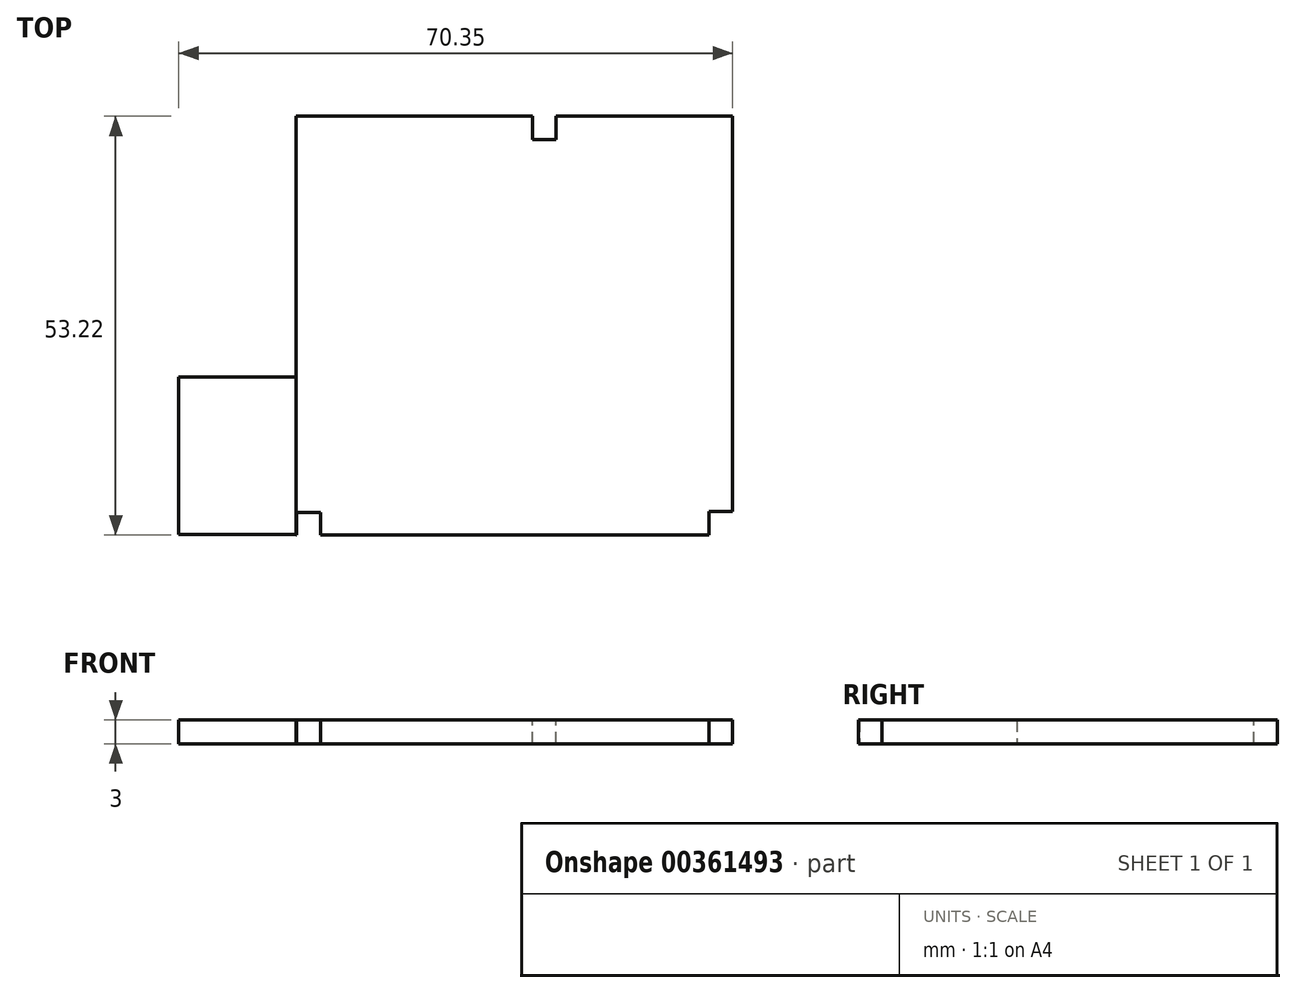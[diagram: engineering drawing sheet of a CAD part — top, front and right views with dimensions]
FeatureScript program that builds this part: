
annotation { "Feature Type Name" : "Feature", "Feature Type Description" : "" }
export const myFeature = defineFeature(function(context is Context, id is Id, definition is map)
    precondition{}
    {
        {
            var Q0;
            Q0=qCreatedBy(makeId("Top.planeOp"),FACE);
            var sketch = newSketch(context, id + "F0", { "sketchPlane" : qUnion([Q0])});
            skLineSegment(sketch, "E0.bottom", {"start": v(-28.37, -22.66) * mm, "end": v(27.04, -22.66) * mm});
            skLineSegment(sketch, "E0.top", {"start": v(-28.37, 30.56) * mm, "end": v(27.04, 30.56) * mm});
            skLineSegment(sketch, "E0.left", {"start": v(-28.37, -22.66) * mm, "end": v(-28.37, 30.56) * mm});
            skLineSegment(sketch, "E0.right", {"start": v(27.04, -22.66) * mm, "end": v(27.04, 30.56) * mm});
            skSolve(sketch);
        }
        {
            var Q0;
            Q0=makeQuery(id+"F0.imprint","IMPRINT",FACE,{"disambiguationData":[TD([[makeQuery(id+"F0.imprint","IMPRINT",EDGE,{"derivedFrom":sQuery(id+"F0.wireOp",EDGE,"E0.bottom")}),1.0]])]});
            var sketch = newSketch(context, id + "F1", { "sketchPlane" : qUnion([Q0])});
            skLineSegment(sketch, "E1.bottom", {"start": v(-43.31, -2.56) * mm, "end": v(-28.31, -2.56) * mm});
            skLineSegment(sketch, "E1.top", {"start": v(-43.31, -22.56) * mm, "end": v(-28.31, -22.56) * mm});
            skLineSegment(sketch, "E1.left", {"start": v(-43.31, -2.56) * mm, "end": v(-43.31, -22.56) * mm});
            skLineSegment(sketch, "E1.right", {"start": v(-28.31, -2.56) * mm, "end": v(-28.31, -22.56) * mm});
            skSolve(sketch);
        }
        {
            var Q0;
            Q0=qCreatedBy(makeId("Top.planeOp"),FACE);
            var sketch = newSketch(context, id + "F2", { "sketchPlane" : qUnion([Q0])});
            skLineSegment(sketch, "E2.bottom", {"start": v(-28.31, -22.76) * mm, "end": v(-25.31, -22.76) * mm});
            skLineSegment(sketch, "E2.top", {"start": v(-28.31, -19.76) * mm, "end": v(-25.31, -19.76) * mm});
            skLineSegment(sketch, "E2.left", {"start": v(-28.31, -22.76) * mm, "end": v(-28.31, -19.76) * mm});
            skLineSegment(sketch, "E2.right", {"start": v(-25.31, -22.76) * mm, "end": v(-25.31, -19.76) * mm});
            skLineSegment(sketch, "E3.bottom", {"start": v(27.04, -22.66) * mm, "end": v(24.04, -22.66) * mm});
            skLineSegment(sketch, "E3.top", {"start": v(27.04, -19.66) * mm, "end": v(24.04, -19.66) * mm});
            skLineSegment(sketch, "E3.left", {"start": v(27.04, -22.66) * mm, "end": v(27.04, -19.66) * mm});
            skLineSegment(sketch, "E3.right", {"start": v(24.04, -22.66) * mm, "end": v(24.04, -19.66) * mm});
            skLineSegment(sketch, "E4.bottom", {"start": v(1.63, 30.56) * mm, "end": v(4.63, 30.56) * mm});
            skLineSegment(sketch, "E4.top", {"start": v(1.63, 27.56) * mm, "end": v(4.63, 27.56) * mm});
            skLineSegment(sketch, "E4.left", {"start": v(1.63, 30.56) * mm, "end": v(1.63, 27.56) * mm});
            skLineSegment(sketch, "E4.right", {"start": v(4.63, 30.56) * mm, "end": v(4.63, 27.56) * mm});
            skSolve(sketch);
        }
        {
            var Q0;
            Q0=makeQuery(id+"F0.imprint","IMPRINT",FACE,{"disambiguationData":[TD([[makeQuery(id+"F0.imprint","IMPRINT",EDGE,{"derivedFrom":sQuery(id+"F0.wireOp",EDGE,"E0.bottom")}),1.0]])]});
            var Q1;
            {var subQ0=sQuery(id+"F1.wireOp",EDGE,"E1.left");Q1=makeQuery(id+"F1.imprint","IMPRINT",FACE,{"disambiguationData":[TD([[makeQuery(id+"F1.imprint","IMPRINT",EDGE,{"derivedFrom":subQ0}),1.0]])]});}
            extrude(context, id + "F3", {"entities" : qUnion([Q0, Q1]), "depth" : 3 * mm});
        }
        {
            var Q0;
            Q0=makeQuery(id+"F2.imprint","IMPRINT",FACE,{"disambiguationData":[TD([[makeQuery(id+"F2.imprint","IMPRINT",EDGE,{"derivedFrom":sQuery(id+"F2.wireOp",EDGE,"E4.bottom")}),-1.0]])]});
            var Q1;
            Q1=makeQuery(id+"F2.imprint","IMPRINT",FACE,{"disambiguationData":[TD([[makeQuery(id+"F2.imprint","IMPRINT",EDGE,{"derivedFrom":sQuery(id+"F2.wireOp",EDGE,"E2.bottom")}),1.0]])]});
            var Q2;
            Q2=makeQuery(id+"F2.imprint","IMPRINT",FACE,{"disambiguationData":[TD([[makeQuery(id+"F2.imprint","IMPRINT",EDGE,{"derivedFrom":sQuery(id+"F2.wireOp",EDGE,"E3.bottom")}),-1.0]])]});
            extrude(context, id + "F4", {"entities" : qUnion([Q0, Q1, Q2]), "operationType" : NewBodyOperationType.ADD, "depth" : 8.2 * mm});
        }
        {
            var Q0;
            Q0=makeQuery(id+"F4.opExtrude","CAP_FACE",FACE,{"disambiguationData":[OSD([sQuery(id+"F2.wireOp",EDGE,"E4.bottom"),sQuery(id+"F2.wireOp",EDGE,"E4.top"),sQuery(id+"F2.wireOp",EDGE,"E4.left"),sQuery(id+"F2.wireOp",EDGE,"E4.right")])],"isStart":false});
            extrude(context, id + "F5", {"entities" : qUnion([Q0]), "operationType" : NewBodyOperationType.ADD, "oppositeDirection" : true, "depth" : 11.8 * mm});
        }
        {
            var Q0;
            Q0=makeQuery(id+"F4.opExtrude","CAP_FACE",FACE,{"disambiguationData":[OSD([sQuery(id+"F2.wireOp",EDGE,"E4.bottom"),sQuery(id+"F2.wireOp",EDGE,"E4.top"),sQuery(id+"F2.wireOp",EDGE,"E4.left"),sQuery(id+"F2.wireOp",EDGE,"E4.right")])],"isStart":false});
            var sketch = newSketch(context, id + "F6", { "sketchPlane" : qUnion([Q0])});
            skLineSegment(sketch, "E5.bottom", {"start": v(4.63, 30.56) * mm, "end": v(1.63, 30.56) * mm});
            skLineSegment(sketch, "E5.top", {"start": v(4.63, 27.56) * mm, "end": v(1.63, 27.56) * mm});
            skLineSegment(sketch, "E5.left", {"start": v(4.63, 30.56) * mm, "end": v(4.63, 27.56) * mm});
            skLineSegment(sketch, "E5.right", {"start": v(1.63, 30.56) * mm, "end": v(1.63, 27.56) * mm});
            skSolve(sketch);
        }
        {
            var Q0;
            Q0=makeQuery(id+"F6.imprint","IMPRINT",FACE,{"disambiguationData":[TD([[makeQuery(id+"F6.imprint","IMPRINT",EDGE,{"derivedFrom":sQuery(id+"F6.wireOp",EDGE,"E5.bottom")}),-1.0]])]});
            extrude(context, id + "F7", {"entities" : qUnion([Q0]), "operationType" : NewBodyOperationType.ADD, "oppositeDirection" : true, "depth" : 18.4 * mm});
        }
        {
            var Q0;
            Q0=makeQuery(id+"F4.opExtrude","CAP_FACE",FACE,{"disambiguationData":[OSD([sQuery(id+"F2.wireOp",EDGE,"E4.bottom"),sQuery(id+"F2.wireOp",EDGE,"E4.top"),sQuery(id+"F2.wireOp",EDGE,"E4.left"),sQuery(id+"F2.wireOp",EDGE,"E4.right")])],"isStart":false});
            extrude(context, id + "F8", {"entities" : qUnion([Q0]), "operationType" : NewBodyOperationType.REMOVE, "oppositeDirection" : true, "depth" : 18.4 * mm});
        }
        {
            var Q0;
            Q0=makeQuery(id+"F4.opExtrude","CAP_FACE",FACE,{"disambiguationData":[OSD([sQuery(id+"F2.wireOp",EDGE,"E2.bottom"),sQuery(id+"F2.wireOp",EDGE,"E2.top"),sQuery(id+"F2.wireOp",EDGE,"E2.left"),sQuery(id+"F2.wireOp",EDGE,"E2.right")])],"isStart":false});
            extrude(context, id + "F9", {"entities" : qUnion([Q0]), "operationType" : NewBodyOperationType.REMOVE, "oppositeDirection" : true, "depth" : 11.5 * mm});
        }
        {
            var Q0;
            Q0=makeQuery(id+"F4.opExtrude","CAP_FACE",FACE,{"disambiguationData":[OSD([sQuery(id+"F2.wireOp",EDGE,"E3.bottom"),sQuery(id+"F2.wireOp",EDGE,"E3.top"),sQuery(id+"F2.wireOp",EDGE,"E3.left"),sQuery(id+"F2.wireOp",EDGE,"E3.right")])],"isStart":false});
            extrude(context, id + "F10", {"entities" : qUnion([Q0]), "operationType" : NewBodyOperationType.REMOVE, "oppositeDirection" : true, "depth" : 25 * mm});
        }
    });
